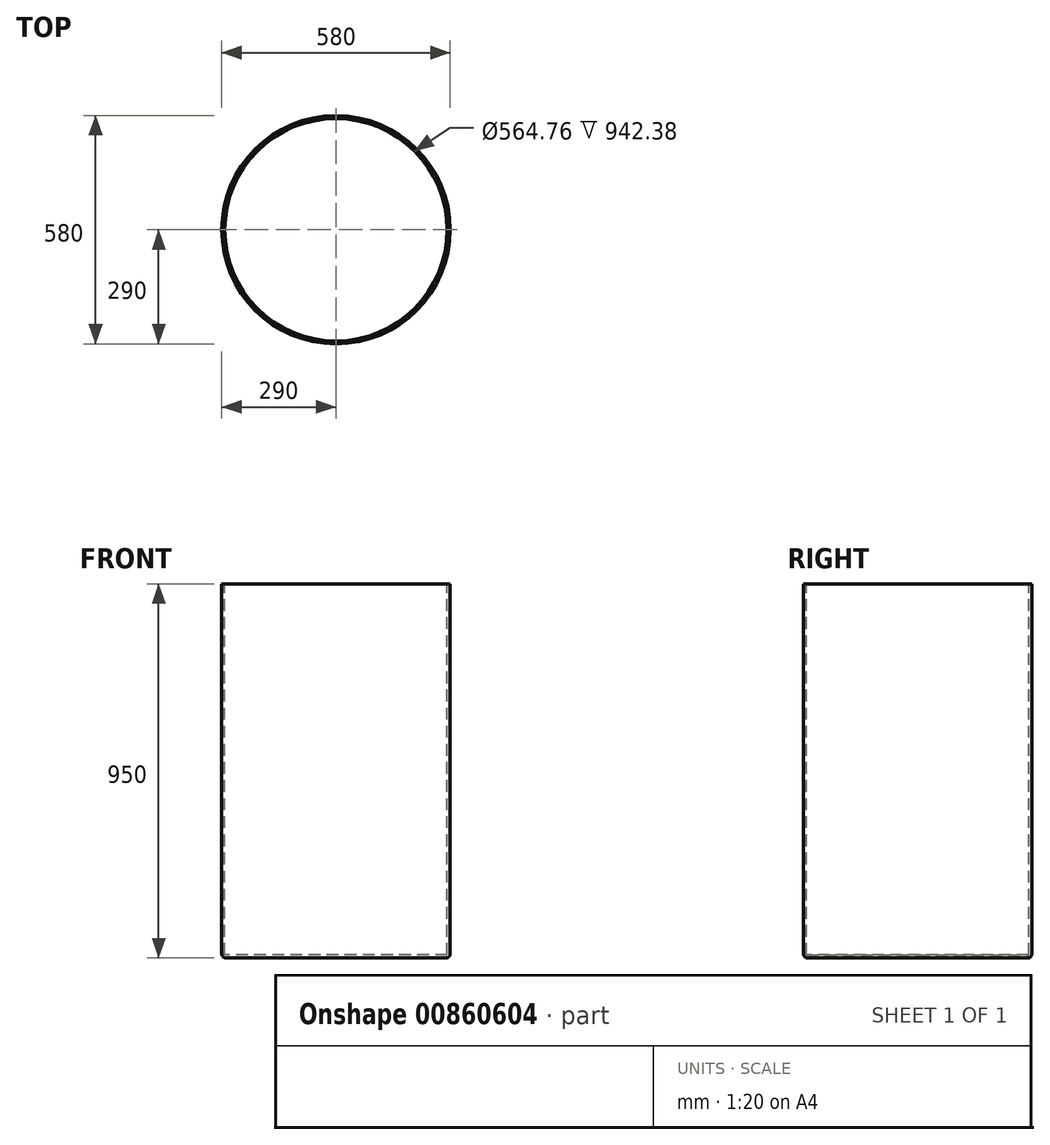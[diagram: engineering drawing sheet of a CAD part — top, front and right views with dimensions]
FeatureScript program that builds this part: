
annotation { "Feature Type Name" : "Feature", "Feature Type Description" : "" }
export const myFeature = defineFeature(function(context is Context, id is Id, definition is map)
    precondition{}
    {
        {
            var Q0;
            Q0=qCreatedBy(makeId("Top.planeOp"),FACE);
            var sketch = newSketch(context, id + "F0", { "sketchPlane" : qUnion([Q0])});
            skCircle(sketch, "E0", {"center": v(0, 0) * mm, "radius": 290 * mm});
            skSolve(sketch);
        }
        {
            var Q0;
            Q0 = qSketchRegion(id + "F0", true);
            extrude(context, id + "F1", {"entities" : qUnion([Q0]), "oppositeDirection" : true, "depth" : 950 * mm, "offsetDistance" : 25.4 * mm});
        }
        {
            var Q0;
            Q0=makeQuery(id+"F1.opExtrude","CAP_FACE",FACE,{"disambiguationData":[OSD([sQuery(id+"F0.wireOp",EDGE,"E0")])],"isStart":true});
            shell(context, id + "F2", {"entities" : qUnion([Q0]), "thickness" : 7.62 * mm});
        }
        {
            var Q0;
            Q0=makeQuery(id+"F1.opExtrude","CAP_EDGE",EDGE,{"disambiguationData":[OSD([sQuery(id+"F0.wireOp",EDGE,"E0")])],"isStart":false});
            fillet(context, id + "F3", {"entities" : qUnion([Q0]), "radius" : 10 * mm, "tangentPropagation" : true, "allowEdgeOverflow" : false});
        }
    });
